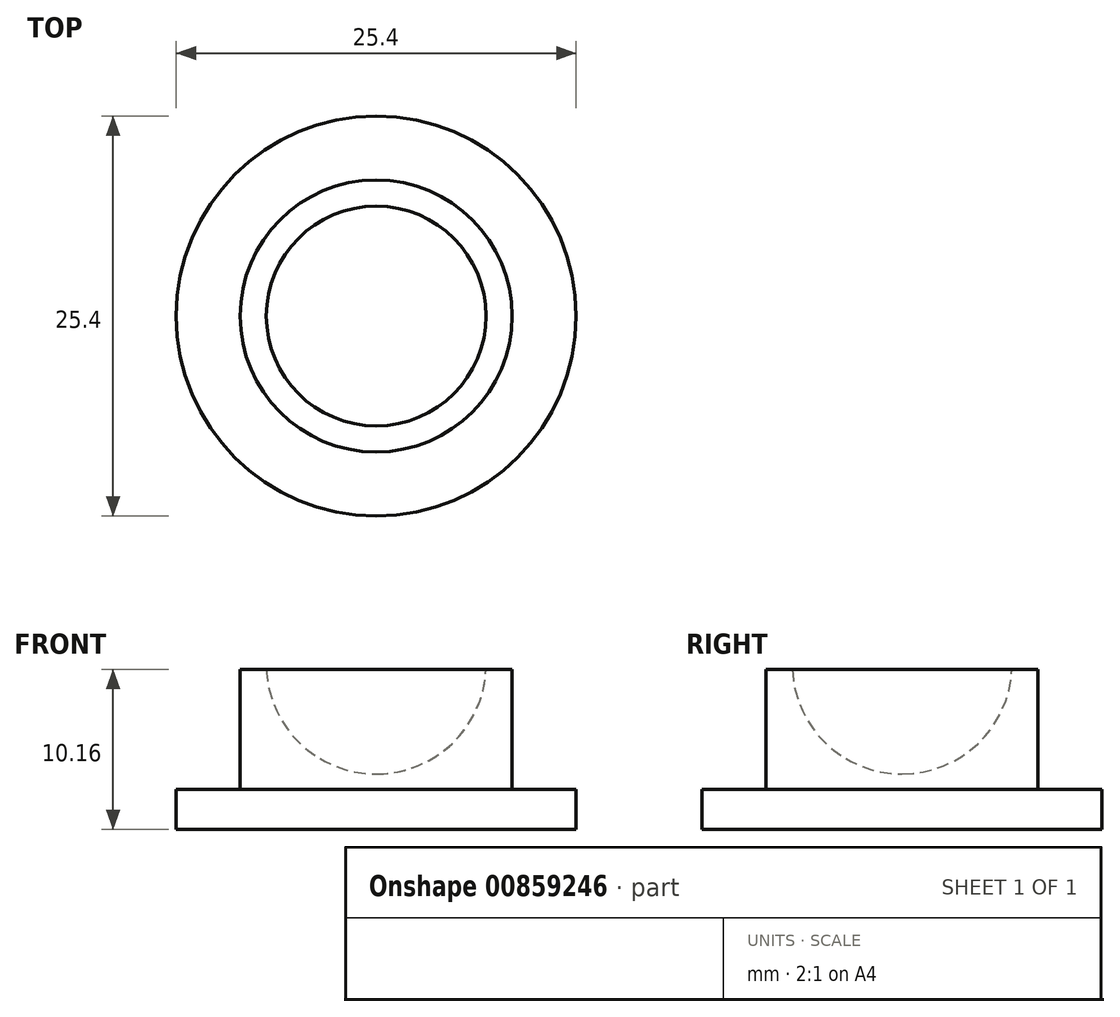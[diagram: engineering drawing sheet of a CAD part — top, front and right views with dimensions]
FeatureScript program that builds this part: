
annotation { "Feature Type Name" : "Feature", "Feature Type Description" : "" }
export const myFeature = defineFeature(function(context is Context, id is Id, definition is map)
    precondition{}
    {
        {
            var Q0;
            Q0=qCreatedBy(makeId("Top.planeOp"),FACE);
            var sketch = newSketch(context, id + "F0", { "sketchPlane" : qUnion([Q0])});
            skCircle(sketch, "E0", {"center": v(0, 0) * mm, "radius": 12.7 * mm});
            skCircle(sketch, "E1", {"center": v(0, 0) * mm, "radius": 8.64 * mm});
            skSolve(sketch);
        }
        {
            var Q0;
            Q0=makeQuery(id+"F0.imprint","IMPRINT",FACE,{"disambiguationData":[TD([[makeQuery(id+"F0.imprint","IMPRINT",EDGE,{"derivedFrom":sQuery(id+"F0.wireOp",EDGE,"E0")}),1.0]])]});
            var Q1;
            Q1=makeQuery(id+"F0.imprint","IMPRINT",FACE,{"disambiguationData":[TD([[makeQuery(id+"F0.imprint","IMPRINT",EDGE,{"derivedFrom":sQuery(id+"F0.wireOp",EDGE,"E1")}),1.0]])]});
            extrude(context, id + "F1", {"entities" : qUnion([Q0, Q1]), "oppositeDirection" : true, "depth" : 2.54 * mm, "offsetDistance" : 25.4 * mm});
        }
        {
            var Q0;
            Q0=makeQuery(id+"F0.imprint","IMPRINT",FACE,{"disambiguationData":[TD([[makeQuery(id+"F0.imprint","IMPRINT",EDGE,{"derivedFrom":sQuery(id+"F0.wireOp",EDGE,"E1")}),1.0]])]});
            extrude(context, id + "F2", {"entities" : qUnion([Q0]), "operationType" : NewBodyOperationType.ADD, "depth" : 7.62 * mm, "offsetDistance" : 25.4 * mm});
        }
        {
            var Q0;
            Q0=qCreatedBy(makeId("Front.planeOp"),FACE);
            var sketch = newSketch(context, id + "F3", { "sketchPlane" : qUnion([Q0])});
            skPoint(sketch, "E2.first.point", {"position": v(0, 0) * mm});
            skArc(sketch, "E3", {"start": v(0, 0.98) * mm, "mid": v(6.99, 7.96) * mm, "end": v(0, 14.95) * mm});
            skLineSegment(sketch, "E4", {"start": v(0, 14.95) * mm, "end": v(0, 0.98) * mm});
            skLineSegment(sketch, "E5", {"start": v(0, 26.1) * mm, "end": v(0, -15.66) * mm});
            skSolve(sketch);
        }
        {
            var Q0;
            {var subQ0=sQuery(id+"F3.wireOp",EDGE,"E3");Q0=makeQuery(id+"F3.imprint","IMPRINT",FACE,{"disambiguationData":[TD([[makeQuery(id+"F3.imprint","IMPRINT",EDGE,{"derivedFrom":subQ0}),1.0]])]});}
            var Q1;
            Q1=sQuery(id+"F3.wireOp",EDGE,"E5");
            revolve(context, id + "F4", {"operationType" : NewBodyOperationType.REMOVE, "surfaceOperationType" : NewSurfaceOperationType.NEW, "entities" : qUnion([Q0]), "axis" : qUnion([Q1]), "revolveType" : RevolveType.FULL});
        }
    });
